# Revit family: M_Ryterna_TLP HL wind_door
name_source: partatom
category: Doors
revit_build: Autodesk Revit 2018 (Build: 20190510_1515(x64)
units: mm (PartAtom-declared; Revit-internal decimal feet)

## family parameters
Always vertical = Yes
Cut with Voids When Loaded = No
Host = Wall
OmniClass Number = 23.30.10.00
OmniClass Title = Doors
Room Calculation Point = No
Shared = No

## types (1)
- TLP HL H3000W3000
    10th Segment Windows = No
    2nd Segment Windows = No
    3rd Segment Windows = No
    4th Segment Windows = No
    5th Segment Windows = No
    6th Segment Windows = No
    7th Segment Windows = No
    8th Segment Windows = No
    9th Segment Windows = No
    Beam H = 100 mm  [stored 0.328084 ft]
    Beam Material = Steel, Galvanized
    Bottom Gasket Material = Gasket Rubber, Black
    Clearance Zone = Yes
    Desired Window Quantity = 0
    Door Bottom Offset = 30 mm  [stored 0.0984252 ft]
    Door Height = 2980 mm
    Door Inset = 15 mm  [stored 0.0492126 ft]
    Door Type Color Material = M_Garage Door : RAL 9016/RAL 9002
    F = 50 mm  [stored 0.164042 ft]
    Guide Track Material = Steel, Galvanized
    HD = 2500 mm  [stored 8.2021 ft]
    HD_True = 2500 mm  [stored 8.2021 ft]
    Height = 3000 mm  [stored 9.84252 ft]
    Height_True = 3000 mm  [stored 9.84252 ft]
    Horizontal C Track Material = Steel, Galvanized
    Lifting Assembly Angle = 90.00°
    Lifting Assembly Horizontal Shift = 0 mm  [stored 0 ft]
    Lifting Type A = M_Lifting Assembly_HL : 1
    Lifting Type B = M_Lifting Assembly_HL : 2
    Lifting Type C = M_Lifting Assembly_HL : 3
    Lifting Type D = M_Lifting Assembly_HL : 4
    Lower Mounted Shaft = No
    Lower Mounted Shaft Clearance Zone = No
    Lower Mounted Shaft_True = No
    Manufacturer = UAB “RYTERNA GROUP”
    Optimal Window Quantity = 3
    PO Host Position = 200 mm  [stored 0.656168 ft]
    Power Operator Position = , : None
    Power Operator Position Left = , : Right
    Power Operator Position Right = , : Left
    Pulley Material = Steel, Galvanized
    R Track = 358 mm  [stored 1.17454 ft]
    Reel Material = Steel, Galvanized
    Regular Clearance Zone = Yes
    Rod Material = Steel, Galvanized
    Roller Holder Material = Steel, Galvanized
    Rough Height = 3010 mm  [stored 9.87533 ft]
    Rough Width = 3040 mm  [stored 9.97375 ft]
    Slab Slope = 0.00°
    Slab Slope_True = 0.00°
    Spring Holder Material = Steel, Galvanized
    Spring Material = Steel, Galvanized
    Thickness = 40 mm  [stored 0.131234 ft]
    Top Gasket Material = Gasket Rubber, Black
    Track Additional Extension = 1880 mm
    Track Height = 3320 mm  [stored 10.8924 ft]
    Triangle Connection Material = Steel, Galvanized
    Triangle Mounting Plate Material = Steel, Galvanized
    Type = - : No Windows
    URL = https://www.ryterna.eu
    Vertical L Profile Material = Steel, Galvanized
    Wall Closure = By host
    Warning Message = No
    Wicket Door Position = _ : No Door
    Wicket Door Position Center = _ : Center
    Wicket Door Position Left = _ : Left
    Wicket Door Position Number = 0
    Wicket Door Position Right = _ : Right
    Wicket Door Swing Direction = . : Right
    Wicket Door Swing Direction Left = . : Left
    Wicket Door Swing Direction Right = . : Right
    Wicket Door Swing Direction Visible = Yes
    Wicket Door Swing Left = No
    Width = 3000 mm  [stored 9.84252 ft]
    Width for Operator = 3000 mm  [stored 9.84252 ft]
    Width_True = 3000 mm  [stored 9.84252 ft]
    Window Type Number = 0
    Window Type Oval = - : Oval
    Window Type Rectangular = - : Rectangular
    Window Type Rectangular Narrow = - : Rectangular Narrow
    Zone Left Lower PO Thickness = -1600 mm  [stored -5.24934 ft]
    Zone Left Upper PO Thickness = -1600 mm  [stored -5.24934 ft]
    Zone Lower PO Depth = 600 mm  [stored 1.9685 ft]
    Zone Right Lower PO Thickness = 1600 mm  [stored 5.24934 ft]
    Zone Right Upper PO Thickness = 1600 mm  [stored 5.24934 ft]
    Zone Sloped Thickness = 83 mm  [stored 0.27231 ft]
    Zone Upper PO Depth = 300 mm  [stored 0.984252 ft]
    Zone Vertical Thickness = 155 mm  [stored 0.50853 ft]

note: [stored X ft] marks values corroborated as IEEE doubles in the binary element streams (Revit-internal decimal feet)

## geometry (parser evidence)
native form markers: Blend x12, Extrusion x4, Sweep x102
no freeform markers — native parametric forms only
